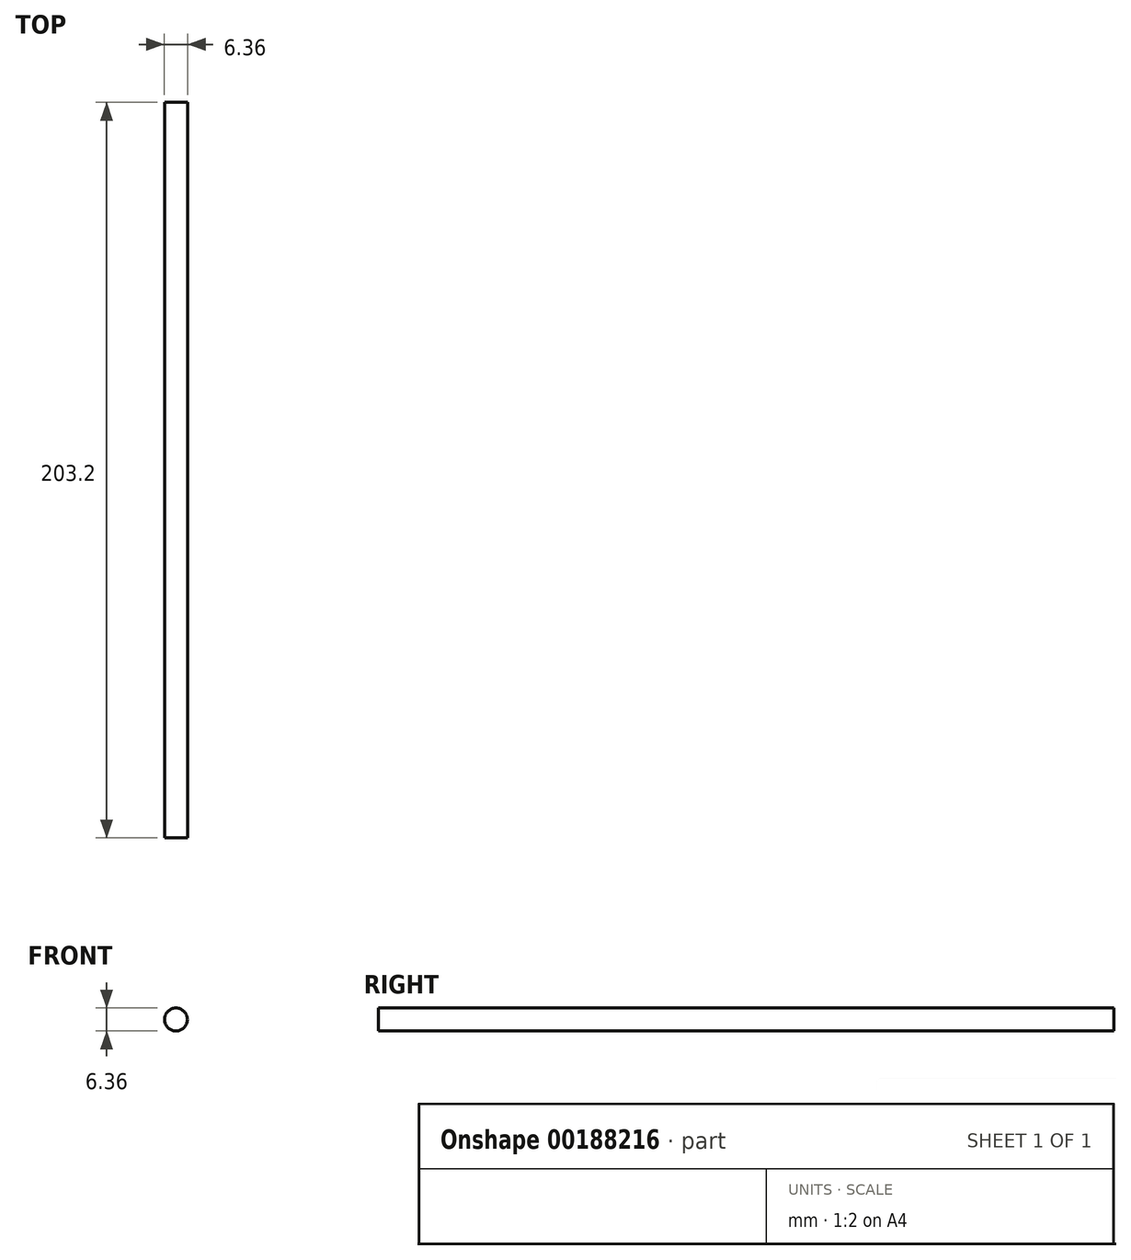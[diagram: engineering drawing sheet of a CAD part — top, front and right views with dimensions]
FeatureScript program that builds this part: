
annotation { "Feature Type Name" : "Feature", "Feature Type Description" : "" }
export const myFeature = defineFeature(function(context is Context, id is Id, definition is map)
    precondition{}
    {
        {
            var Q0;
            Q0=qCreatedBy(makeId("Front.planeOp"),FACE);
            var sketch = newSketch(context, id + "F0", { "sketchPlane" : qUnion([Q0])});
            skCircle(sketch, "E0", {"center": v(0, 0) * mm, "radius": 3.18 * mm});
            skSolve(sketch);
        }
        {
            var Q0;
            Q0 = qSketchRegion(id + "F0", true);
            extrude(context, id + "F1", {"entities" : qUnion([Q0]), "endBound" : BoundingType.SYMMETRIC, "depth" : 203.2 * mm});
        }
    });
